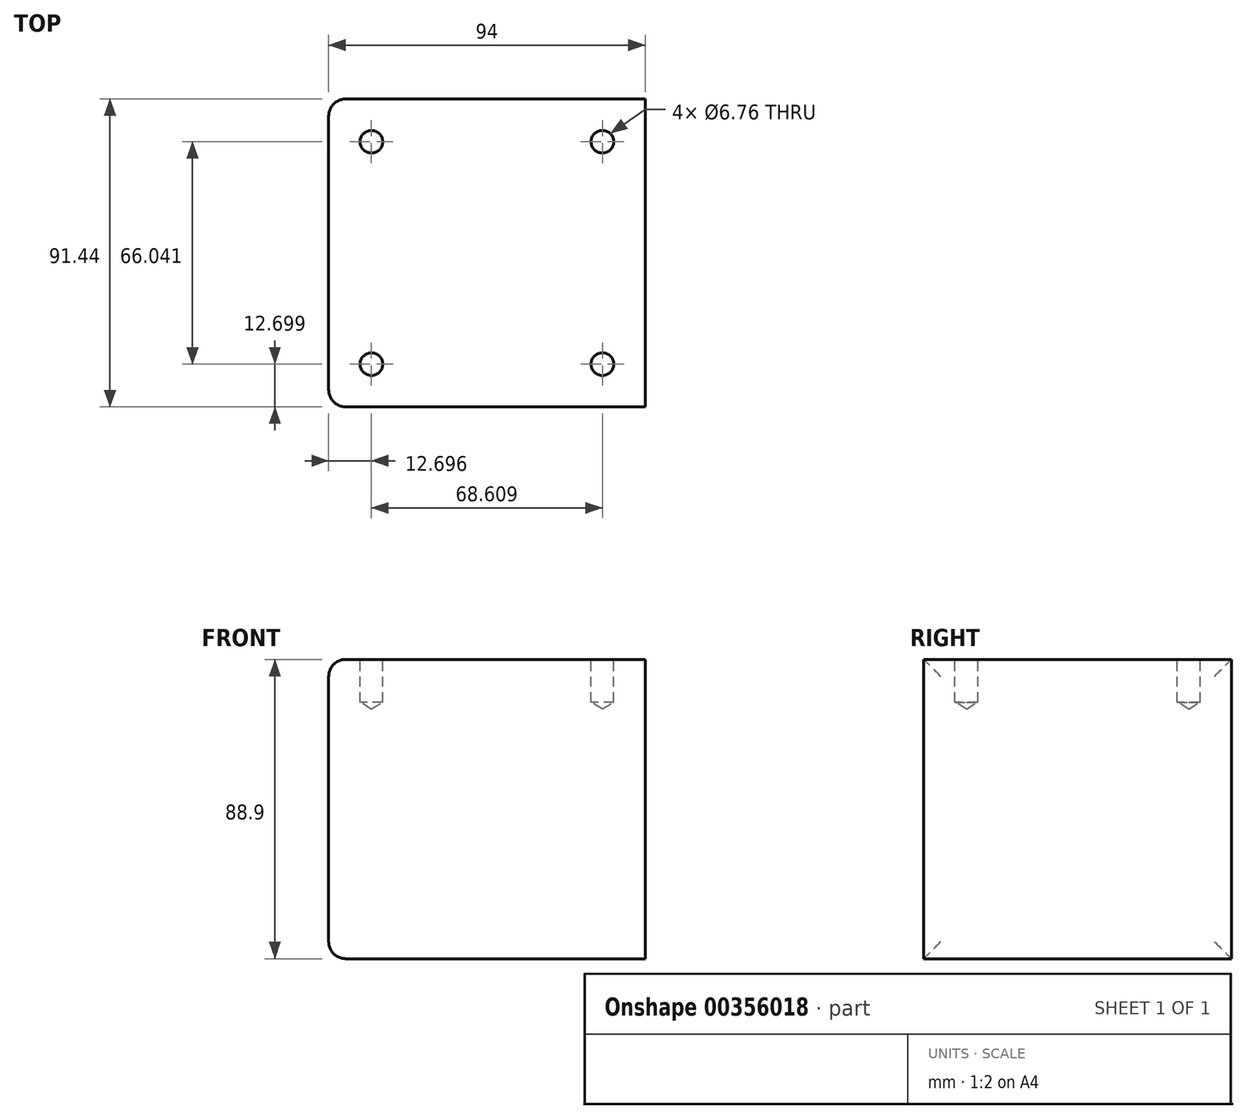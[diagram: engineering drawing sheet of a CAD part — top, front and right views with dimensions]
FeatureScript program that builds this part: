
annotation { "Feature Type Name" : "Feature", "Feature Type Description" : "" }
export const myFeature = defineFeature(function(context is Context, id is Id, definition is map)
    precondition{}
    {
        {
            var Q0;
            Q0=qCreatedBy(makeId("Top.planeOp"),FACE);
            var sketch = newSketch(context, id + "F0", { "sketchPlane" : qUnion([Q0])});
            skLineSegment(sketch, "E0.bottom", {"start": v(47, 45.72) * mm, "end": v(-47, 45.72) * mm});
            skLineSegment(sketch, "E0.top", {"start": v(47, -45.72) * mm, "end": v(-47, -45.72) * mm});
            skLineSegment(sketch, "E0.left", {"start": v(47, 45.72) * mm, "end": v(47, -45.72) * mm});
            skLineSegment(sketch, "E0.right", {"start": v(-47, 45.72) * mm, "end": v(-47, -45.72) * mm});
            skPoint(sketch, "E0.middle", {"position": v(0, 0) * mm});
            skSolve(sketch);
        }
        {
            var Q0;
            Q0 = qSketchRegion(id + "F0", true);
            extrude(context, id + "F1", {"entities" : qUnion([Q0]), "depth" : 88.9 * mm});
        }
        {
            var Q0;
            Q0=makeQuery(id+"F1.opExtrude","CAP_FACE",FACE,{"disambiguationData":[OSD([sQuery(id+"F0.wireOp",EDGE,"E0.bottom"),sQuery(id+"F0.wireOp",EDGE,"E0.top"),sQuery(id+"F0.wireOp",EDGE,"E0.left"),sQuery(id+"F0.wireOp",EDGE,"E0.right")])],"isStart":false});
            var sketch = newSketch(context, id + "F2", { "sketchPlane" : qUnion([Q0])});
            skPoint(sketch, "E1", {"position": v(-34.3, 33.02) * mm});
            skPoint(sketch, "E2", {"position": v(34.3, 33.02) * mm});
            skPoint(sketch, "E3", {"position": v(34.3, -33.02) * mm});
            skPoint(sketch, "E4", {"position": v(-34.3, -33.02) * mm});
            skSolve(sketch);
        }
        {
            var Q0;
            Q0=sQuery(id+"F2.wireOp",VERTEX,"E1");
            var Q1;
            Q1=sQuery(id+"F2.wireOp",VERTEX,"E2");
            var Q2;
            Q2=sQuery(id+"F2.wireOp",VERTEX,"E3");
            var Q3;
            Q3=sQuery(id+"F2.wireOp",VERTEX,"E4");
            var Q4;
            Q4=makeQuery(id+"F1.opExtrude","SWEPT_BODY",BODY,{"disambiguationData":[OSD([sQuery(id+"F0.wireOp",EDGE,"E0.bottom"),sQuery(id+"F0.wireOp",EDGE,"E0.top"),sQuery(id+"F0.wireOp",EDGE,"E0.left"),sQuery(id+"F0.wireOp",EDGE,"E0.right")])]});
            hole(context, id + "F3", {"style" : HoleStyle.SIMPLE, "endStyle" : HoleEndStyle.BLIND, "standardTappedOrClearance" : lookupTablePath({ "standard" : "ANSI", "fit" : "Normal (ASME)", "size" : "1/4", "type" : "Clearance" }), "standardBlindInLast" : lookupTablePath({ "fit" : "Free", "standard" : "ANSI", "size" : "1/4", "type" : "Clearance" }), "holeDiameter" : 6.76 * mm, "holeDepth" : 12.7 * mm, "isTappedThrough" : true, "tappedDepth" : 12.7 * mm, "tapClearance" : 3, "locations" : qUnion([Q0, Q1, Q2, Q3]), "scope" : qUnion([Q4])});
        }
        {
            var Q0;
            Q0=qCreatedBy(makeId("Top.planeOp"),FACE);
            var sketch = newSketch(context, id + "F4", { "sketchPlane" : qUnion([Q0])});
            skFitSpline(sketch, "E5", {"points": [v(-116.53, 39.17) * mm, v(-95.3, 49.88) * mm, v(-84.9, 32.12) * mm, v(-96.35, 7.63) * mm, v(-113.75, -20.22) * mm, v(-111.88, -32.22) * mm, v(-104.55, -42.55) * mm, v(-99.44, -48.26) * mm, v(-80.99, -45.9) * mm, v(-82.2, -54.21) * mm], "startDerivative": vector(173.49, 143.42) * mm, "endDerivative": vector(-61.37, -142) * mm});
            skSolve(sketch);
        }
        {
            var Q0;
            Q0 = qSketchRegion(id + "F4", true);
            var Q1;
            Q1=sQuery(id+"F4.wireOp",EDGE,"E5");
            extrude(context, id + "F5", {"entities" : qUnion([Q0]), "bodyType" : ToolBodyType.SURFACE, "surfaceEntities" : qUnion([Q1]), "depth" : 25.4 * mm});
        }
        {
            var Q0;
            Q0=makeQuery(id+"F1.opExtrude","SWEPT_FACE",FACE,{"disambiguationData":[OSD([sQuery(id+"F0.wireOp",EDGE,"E0.right")])]});
            fillet(context, id + "F6", {"entities" : qUnion([Q0]), "radius" : 5.08 * mm, "tangentPropagation" : true, "allowEdgeOverflow" : false});
        }
    });
